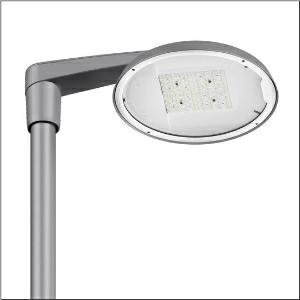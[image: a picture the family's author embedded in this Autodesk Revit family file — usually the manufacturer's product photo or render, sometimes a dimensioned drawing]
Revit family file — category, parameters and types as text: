
# Revit family: dl_r__50_iq_mini___st0_5a_5xa248b41f08me_b712
name_source: partatom
category: Lighting Fixtures
units: mm (PartAtom-declared; Revit-internal decimal feet)

## family parameters
Cut with Voids When Loaded = No
Host = Face
Light Source = No
Part Type = Normal
Room Calculation Point = No
Round Connector Dimension = Use Diameter
Shared = No

## types (1)
- --- (1 x LED, 15660 lm, 101.7 W, 4000K)
    Apparent Load = 102 VA
    CIE Flux Codes = 41 75 97 100 100
    Color Rendering = 70
    Color Temperature = 4000K
    Default Elevation = 1800 mm
    Description = DL® 50 iQ mini, mast luminaire, primary light control with lens, of PMMA, primary optical cover: cover, of toughened safety glass, transparent, light distribution: ST0.5a, light emission: direct distribution, primary light characteristic: asymmetric, installation type: side-entry, post-top, LED, High Power LED, rated luminous flux: 15.660lm, luminous efficacy: 154lm/W, light colour: 740, colour temperature: 4000K, control: optimised constant luminous flux control (CLO 2.0), Desk-Remote (wireless, voltage-free reading and setting of iQ features in the workshop via application-optimized NFC function/RFID function), Light-Fading, Smart-Wire, Night-Set, Lumen-Switch, Temp-Guard, Auto-Match, Street-Remote, mains connection: 230..240V, AC, 50/60Hz, connection cable pre-assembled, cable length: 10,5m, start of lifetime: 102W, end of service life: 111W, reduction: 45W, luminaire housing, of diecast aluminium, powder-coated, Siteco® metallic grey (DB 702S), inclination adjustable: 0°, 5°, 10° (post-top) | 0°, -5°, -10°, -15° (side-entry), please order mast post-top element or mast side-entry element separately, diameter: 500mm, height: 115mm, post-top: for spigot size d x l = 76 x 100mm; with reducer (optional accessory) 60 x 100mm | side-entry: for spigot size d x l = 60 x 100mm; with reducer (optional accessory) 42 x 100mm, protection rating (complete): IP66, insulation class (complete): insulation class II (safety insulation), certification: CE, ENEC, VDE, impact resistance: IK08, permissible operating ambient temperature for outdoor applications: -25..+40°C, standard-compliant lighting for roads and squares, packaging unit: 1 piece

Light Distribution: ST0.5a
    Height = 115 mm
    Lamp = 1 x LED
    Lamp Light Flux = 15660 lm
    Lamp Power = 101.7 W
    Lamp count = 1
    Length = 500 mm
    Luminous efficacy = 154 lm/W
    Manufacturer = Siteco
    ModVariant = No
    Model = 5XA248B41F08ME
    Number of Poles = 1
    OnlyDefault = Yes
    Power Factor = 1
    Product Name = DL® 50 iQ mini | ST0.5a
    Product group = mast luminaire | pylon top
    ProductGroupID = 6100
    Protection Class = Protection class II
    Protection Degree = IP 66
    RLX_Detail_Level = 1
    RLX_Emergency_Light_Flux = 0 lm
    RLX_Emergency_Type = 0
    RLX_Emergency_Type_DB = No
    RlxData = <blob elided: 127649 chars, md5=3609e2b7>
    Socket = socket
    Standby Power = 0 W
    System Light Flux = 15660 lm
    System Power = 102 W
    Type Comments = factory setting: luminous flux: 100 % | dim-lin: 254 | 534 mA
    Type Image = l_1251790.jpg
    URL = http://relux.com
    VarID = @adj_092403
    Voltage = 0 V
    Weight = 0.00 kg
    Width = 0 mm  [stored 0 ft]

note: [stored X ft] marks values corroborated as IEEE doubles in the binary element streams (Revit-internal decimal feet)

## geometry (parser evidence)
native form markers: Blend x4, Sweep x13
no freeform markers — native parametric forms only
